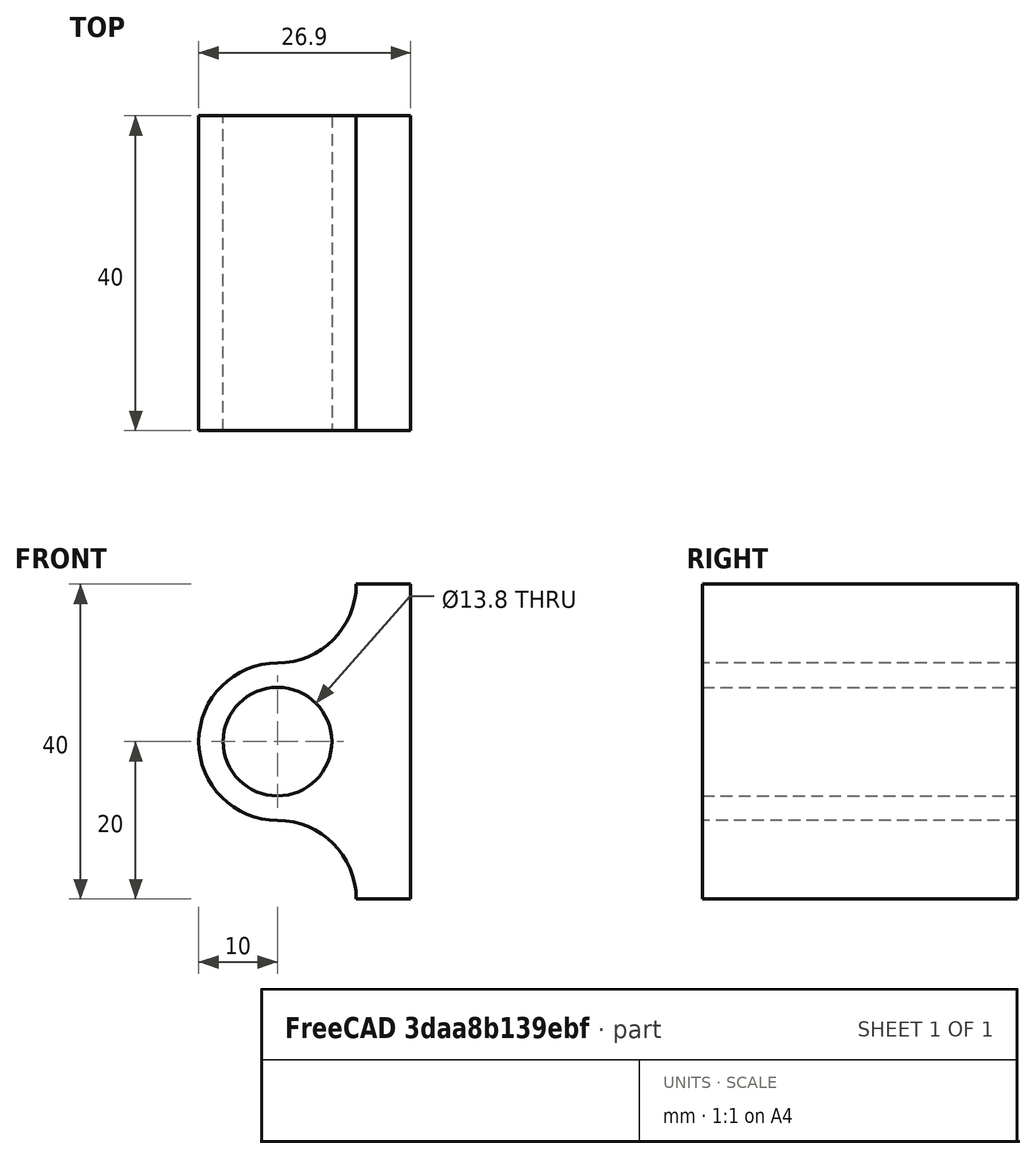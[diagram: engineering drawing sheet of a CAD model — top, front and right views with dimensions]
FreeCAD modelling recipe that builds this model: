
FCSTD DOCUMENT  (FreeCAD 0.19R)
Label: PlotterSled
License: All rights reserved
LicenseURL: http://en.wikipedia.org/wiki/All_rights_reserved
objects: App::DocumentObjectGroup×3, PartDesign::CoordinateSystem×3, App::FeaturePython×1, Sketcher::SketchObject×1, PartDesign::Pad×1, PartDesign::Body×1, App::Part×1
note: 7 computed .brp shape members not serialized (recipe doc carries the construction recipe); baked Part::Feature solids carry a one-line shape summary decoded from their .brp

FEATURE [App::DocumentObjectGroup] Parts
FEATURE [PartDesign::CoordinateSystem] LCS_Origin
  AttacherType = Attacher::AttachEngine3D
  MapMode = 2
  Support = -> [X_Axis]
FEATURE [App::DocumentObjectGroup] Constraints
FEATURE [App::FeaturePython] Variables  # WARN: FeaturePython — macro-defined, semantics opaque (R4)
  Type = App::PropertyContainer
FEATURE [App::DocumentObjectGroup] Configurations
FEATURE [Sketcher::SketchObject] Sketch017
  FullyConstrained = true
  Placement = pos=(0,200,0) rot=(1,0,0;1.5708rad)
  sketch-geometry (9):
    g0: Circle CenterX=21 CenterY=30.7 CenterZ=0 NormalX=0 NormalY=0 NormalZ=1 AngleXU=0 Radius=6.9
    g1: ArcOfCircle CenterX=21 CenterY=30.7 CenterZ=0 NormalX=0 NormalY=0 NormalZ=1 AngleXU=0 Radius=10 StartAngle=1.5708 EndAngle=4.71239
    g2: LineSegment StartX=21 StartY=51.79 StartZ=0 EndX=21 EndY=0 EndZ=0
    g3: LineSegment StartX=3.39 StartY=30.7 StartZ=0 EndX=44.96 EndY=30.7 EndZ=0
    g4: ArcOfCircle CenterX=21 CenterY=50.7 CenterZ=0 NormalX=0 NormalY=0 NormalZ=1 AngleXU=0 Radius=10 StartAngle=4.71239 EndAngle=6.28319
    g5: ArcOfCircle CenterX=21 CenterY=10.7 CenterZ=0 NormalX=0 NormalY=0 NormalZ=1 AngleXU=0 Radius=10 StartAngle=0 EndAngle=1.5708
    g6: LineSegment StartX=37.9 StartY=50.7 StartZ=0 EndX=37.9 EndY=10.7 EndZ=0
    g7: LineSegment StartX=37.9 StartY=10.7 StartZ=0 EndX=31 EndY=10.7 EndZ=0
    g8: LineSegment StartX=31 StartY=50.7 StartZ=0 EndX=37.9 EndY=50.7 EndZ=0
  constraints (29):
    c: Radius(g0) = 6.9
    c: DistanceY(g0) = 30.7
    c: DistanceX(g0) = 21
    c: Coincident(g1,g0)
    c: Vertical(g2)
    c: DistanceX(g2) = 21
    c: PointOnObject(g1,g2)
    c: PointOnObject(g1,g2)
    c: Horizontal(g3)
    c: Distance(g3) = 41.57
    c: DistanceX(g3) = 3.39
    c: DistanceY(g-1,g3) = 30.7
    c: Coincident(g4,g1)
    c: Coincident(g5,g1)
    c: Symmetric(g5,g4,g3)
    c: Radius(g4) = 10
    c: PointOnObject(g4,g2)
    c: Radius(g5) = 10
    c: Distance(g4,g5) = 40
    c: Radius(g1) = 10
    c: Coincident(g6,g7)
    c: Coincident(g7,g5)
    c: Horizontal(g7)
    c: Coincident(g8,g4)
    c: Coincident(g8,g6)
    c: Symmetric(g6,g6,g3)
    c: DistanceX(g5,g6) = 6.9
    c: PointOnObject(g2,g-1)
    c: Distance(g2) = 51.79
FEATURE [PartDesign::Pad] Pad007
  Direction = (1,1,1)
  Length = 40
  Length2 = 100
  Midplane = true
  Placement = pos=(0,200,0) rot=(1,0,0;1.5708rad)
  Profile = -> Sketch017
  Refine = true
  Type = 0
FEATURE [PartDesign::Body] Body007  label="Y_Axis_Sled"
  Group = -> [Sketch017,Pad007]
  Origin = -> Origin007
  Tip = -> Pad007
FEATURE [PartDesign::CoordinateSystem] LCS_1
  AttacherType = Attacher::AttachEngine3D
  AttachmentOffset = pos=(0,0,197) rot=(-0.57735,0.57735,-0.57735;2.0944rad)
  MapMode = 11
  Placement = pos=(21,-17,30.7) rot=(0,0,1;0rad)
  Support = -> [Pad007]
FEATURE [PartDesign::CoordinateSystem] LCS_2
  AttacherType = Attacher::AttachEngine3D
  AttachmentOffset = pos=(30.7,0,0) rot=(0,0,1;-1.5708rad)
  MapMode = 5
  Placement = pos=(37.9,200,30.7) rot=(-0.57735,-0.57735,-0.57735;4.18879rad)
  Support = -> [Pad007]
FEATURE [App::Part] Model
  AssemblyType = Part::Link
  Group = -> [LCS_Origin,Constraints,Variables,Configurations,Body007,LCS_1,LCS_2]
  Origin = -> Origin
  Type = Assembly
